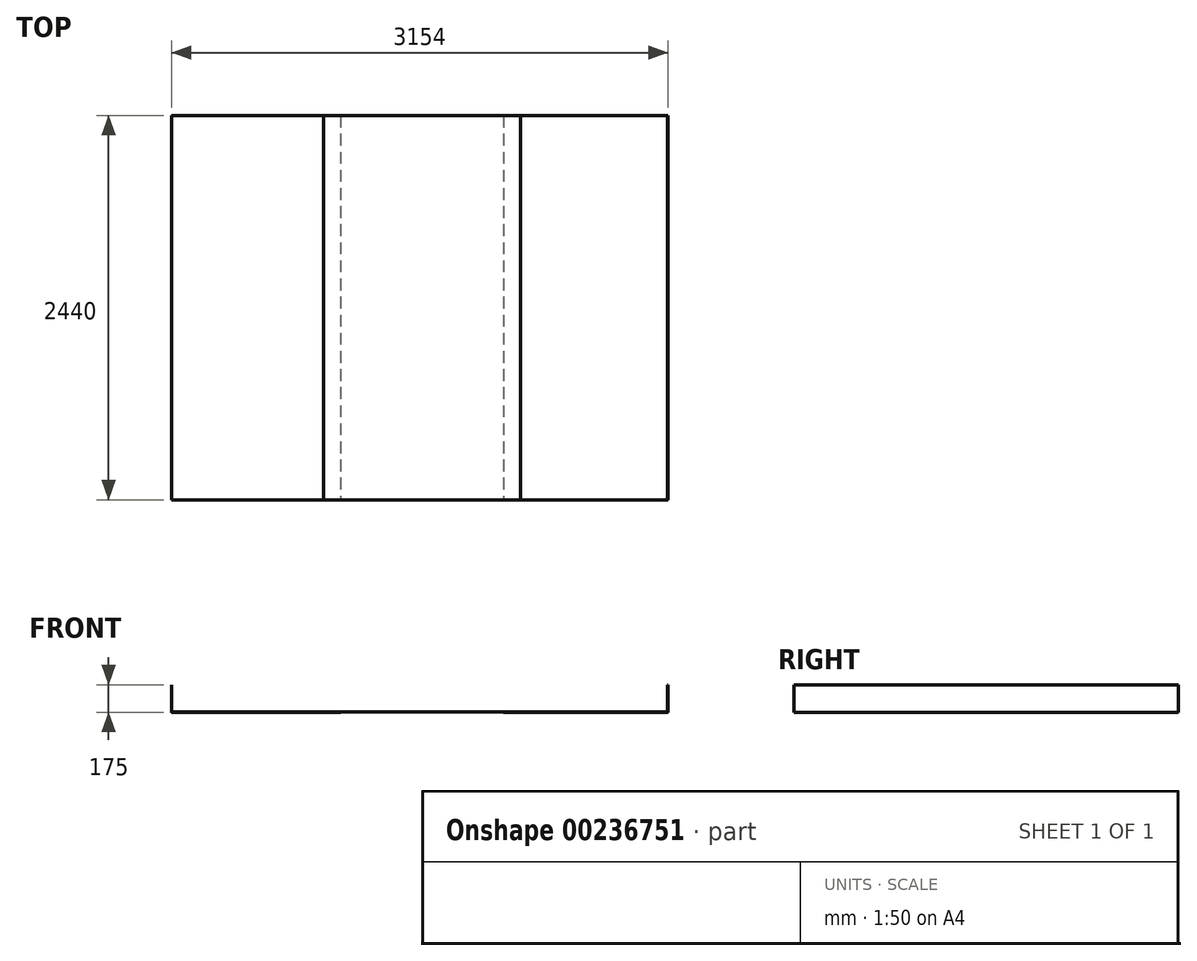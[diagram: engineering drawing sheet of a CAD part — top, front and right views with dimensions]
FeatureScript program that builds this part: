
annotation { "Feature Type Name" : "Feature", "Feature Type Description" : "" }
export const myFeature = defineFeature(function(context is Context, id is Id, definition is map)
    precondition{}
    {
        {
            var Q0;
            Q0=qCreatedBy(makeId("Front.planeOp"),FACE);
            var sketch = newSketch(context, id + "F0", { "sketchPlane" : qUnion([Q0])});
            skLineSegment(sketch, "E0.bottom", {"start": v(3, 0) * mm, "end": v(1075, 0) * mm});
            skLineSegment(sketch, "E0.top", {"start": v(5, 2) * mm, "end": v(1075, 2) * mm});
            skLineSegment(sketch, "E0.right", {"start": v(1075, 0) * mm, "end": v(1075, 2) * mm});
            skLineSegment(sketch, "E1.bottom", {"start": v(0, 0) * mm, "end": v(0, 0) * mm});
            skLineSegment(sketch, "E1.top", {"start": v(2, 175) * mm, "end": v(0, 175) * mm});
            skLineSegment(sketch, "E1.left", {"start": v(2, 5) * mm, "end": v(2, 175) * mm});
            skLineSegment(sketch, "E1.right", {"start": v(0, 3) * mm, "end": v(0, 175) * mm});
            skArc(sketch, "E2.filletArc", {"start": v(2, 5) * mm, "mid": v(2.88, 2.88) * mm, "end": v(5, 2) * mm});
            skPoint(sketch, "E3.visualSharp", {"position": v(0, 0) * mm});
            skArc(sketch, "E3.filletArc", {"start": v(0, 3) * mm, "mid": v(0.88, 0.88) * mm, "end": v(3, 0) * mm});
            skLineSegment(sketch, "E4", {"start": v(2109, 0) * mm, "end": v(3151, 0) * mm});
            skLineSegment(sketch, "E5", {"start": v(3154, 3) * mm, "end": v(3154, 175) * mm});
            skLineSegment(sketch, "E6", {"start": v(3154, 175) * mm, "end": v(3152, 175) * mm});
            skLineSegment(sketch, "E7", {"start": v(3152, 175) * mm, "end": v(3152, 5) * mm});
            skLineSegment(sketch, "E8", {"start": v(3149, 2) * mm, "end": v(2109, 2) * mm});
            skLineSegment(sketch, "E9", {"start": v(2109, 2) * mm, "end": v(2109, 0) * mm});
            skPoint(sketch, "E10.visualSharp", {"position": v(3154, 0) * mm});
            skArc(sketch, "E10.filletArc", {"start": v(3151, 0) * mm, "mid": v(3153.12, 0.88) * mm, "end": v(3154, 3) * mm});
            skPoint(sketch, "E11.visualSharp", {"position": v(3152, 2) * mm});
            skArc(sketch, "E11.filletArc", {"start": v(3149, 2) * mm, "mid": v(3151.12, 2.88) * mm, "end": v(3152, 5) * mm});
            skLineSegment(sketch, "E12.left", {"start": v(844.6, 2) * mm, "end": v(844.6, 2) * mm});
            skLineSegment(sketch, "E12.right", {"start": v(2317.14, 2) * mm, "end": v(2317.14, 2) * mm});
            skLineSegment(sketch, "E13.bottom", {"start": v(2217, 2) * mm, "end": v(967, 2) * mm});
            skLineSegment(sketch, "E13.top", {"start": v(2217, 4) * mm, "end": v(967, 4) * mm});
            skLineSegment(sketch, "E13.left", {"start": v(2217, 2) * mm, "end": v(2217, 4) * mm});
            skLineSegment(sketch, "E13.right", {"start": v(967, 2) * mm, "end": v(967, 4) * mm});
            skSolve(sketch);
        }
        {
            var Q0;
            Q0=makeQuery(id+"F0.imprint","IMPRINT",FACE,{"disambiguationData":[TD([[makeQuery(id+"F0.imprint","IMPRINT",EDGE,{"derivedFrom":sQuery(id+"F0.wireOp",EDGE,"E0.bottom")}),1.0]])]});
            var Q1;
            Q1=makeQuery(id+"F0.imprint","IMPRINT",FACE,{"disambiguationData":[TD([[makeQuery(id+"F0.imprint","IMPRINT",EDGE,{"derivedFrom":sQuery(id+"F0.wireOp",EDGE,"E4")}),1.0]])]});
            var Q2;
            {var subQ0=sQuery(id+"F0.wireOp",EDGE,"E13.bottom");Q2=makeQuery(id+"F0.imprint","IMPRINT",FACE,{"disambiguationData":[TD([[makeQuery(id+"F0.imprint","IMPRINT",EDGE,{"derivedFrom":subQ0}),-1.0]])]});}
            extrude(context, id + "F1", {"entities" : qUnion([Q0, Q1, Q2]), "oppositeDirection" : true, "depth" : 2440 * mm, "offsetDistance" : 25 * mm});
        }
    });
